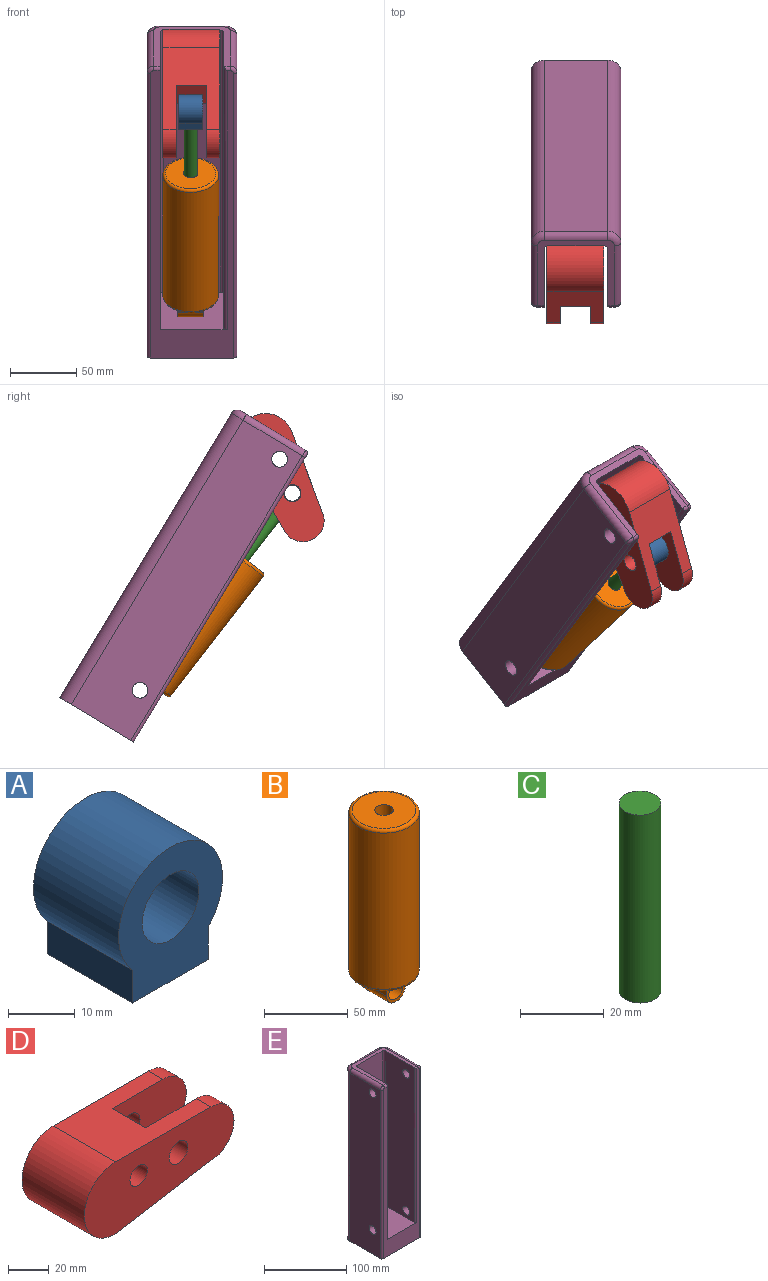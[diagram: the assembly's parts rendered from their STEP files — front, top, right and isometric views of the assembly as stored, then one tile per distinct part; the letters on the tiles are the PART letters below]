
ASSEMBLY  parts=5 mates=5
PART A: 7 faces, bbox 22x18x24.6 mm
  f0: cylinder r=11mm len=22mm, axis (0,1,0), area 921.6mm2, adj f1,f3,f5,f6
  f1: plane 18x6mm, normal (-1,0,0), area 108mm2, adj f0,f2,f5,f6
  f2: plane 18x16mm, normal (0,0,-1), area 288mm2, adj f1,f3,f5,f6
  f3: plane 18x6mm, normal (1,0,0), area 108mm2, adj f0,f2,f5,f6
  f4: cylinder r=6mm len=18mm, axis (0,1,0), area 678.6mm2, adj f5,f6
  f5: plane 24.55x22mm, normal (0,-1,0), area 324.9mm2, adj f0,f1,f2,f3,f4
  f6: plane 24.55x22mm, normal (0,1,0), area 324.9mm2, adj f0,f1,f2,f3,f4
PART B: 13 faces, bbox 45.6x45.6x135 mm
  f0: cylinder r=21.05mm len=114.1mm, axis (0,0,-1), area 15091mm2, adj f3,f4
  f1: plane 38.1x38.1mm, normal (0,0,1), area 1045.1mm2, adj f4,f5
  f2: plane 38.1x38.1mm, normal (0,0,-1), area 820.1mm2, adj f3,f7,f8,f9,f10
  f3: torus R=19.05mm, axis (0,0,1), area 401.2mm2, adj f0,f2
  f4: torus R=19.05mm, axis (0,0,1), area 401.2mm2, adj f0,f1
  f5: cylinder r=5.5mm len=56.1mm, axis (0,0,1), area 1938.7mm2, adj f1,f6
  f6: plane 11x11mm, normal (0,0,1), area 95mm2, adj f5
  f7: plane 20x8.94mm, normal (-1,0,0), area 178.9mm2, adj f2,f9,f10,f11
  f8: plane 20x8.94mm, normal (1,0,0), area 178.9mm2, adj f2,f9,f10,f11
  f9: plane 16.94x16mm, normal (0,-1,0), area 130.5mm2, adj f2,f7,f8,f11,f12
  f10: plane 16.94x16mm, normal (0,1,0), area 130.5mm2, adj f2,f7,f8,f11,f12
  f11: cylinder r=8mm len=20mm, axis (0,1,0), area 502.7mm2, adj f7,f8,f9,f10
  f12: cylinder r=6mm len=20mm, axis (0,1,0), area 754mm2, adj f9,f10
PART C: 3 faces, bbox 10x10x55 mm
  f0: cylinder r=5mm len=55mm, axis (0,0,-1), area 1727.9mm2, adj f1,f2
  f1: plane 10x10mm, normal (0,0,1), area 78.5mm2, adj f0
  f2: plane 10x10mm, normal (0,0,-1), area 78.5mm2, adj f0
PART D: 13 faces, bbox 103.3x43x43 mm
  f0: plane 65.77x43mm, normal (0,0,1), area 2023.1mm2, adj f2,f3,f6,f8,f9,f10,f11,f12
  f1: plane 65.77x43mm, normal (0.16,0,-0.99), area 2051.2mm2, adj f2,f3,f6,f8,f9,f10,f11,f12
  f2: cylinder r=16mm len=32mm, axis (0,1,0), area 502.7mm2, adj f0,f1,f8,f11
  f3: cylinder r=16mm len=32mm, axis (0,1,0), area 502.7mm2, adj f0,f1,f9,f12
  f4: cylinder r=6.46mm len=12.92mm, axis (0,1,0), area 405.7mm2, adj f8,f11
  f5: cylinder r=6.46mm len=12.92mm, axis (0,1,0), area 405.7mm2, adj f9,f12
  f6: cylinder r=21.5mm len=43mm, axis (0,1,0), area 2904.4mm2, adj f0,f1,f8,f9
  f7: cylinder r=6mm len=43mm, axis (0,1,0), area 1621.1mm2, adj f8,f9
  f8: plane 103.27x43mm, normal (0,-1,0), area 3350.4mm2, adj f0,f1,f2,f4,f6,f7
  f9: plane 103.27x43mm, normal (0,1,0), area 3350.4mm2, adj f0,f1,f3,f5,f6,f7
  f10: plane 37.85x23mm, normal (1,0,0), area 870.6mm2, adj f0,f1,f11,f12
  f11: plane 51x37.85mm, normal (0,1,0), area 1493.6mm2, adj f0,f1,f2,f4,f10
  f12: plane 51x37.85mm, normal (0,-1,0), area 1493.6mm2, adj f0,f1,f3,f5,f10
PART E: 30 faces, bbox 69.6x65.8x256.4 mm
  f0: plane 231x52.5mm, normal (1,0,0), area 11900mm2, adj f1,f5,f11,f13,f15,f16,f25
  f1: cylinder r=2.5mm len=231mm, axis (0,0,-1), area 907.1mm2, adj f0,f2,f11,f15
  f2: plane 231x43mm, normal (0,-1,0), area 9933mm2, adj f1,f3,f11,f15
  f3: cylinder r=2.5mm len=231mm, axis (0,0,-1), area 907.1mm2, adj f2,f4,f11,f15
  f4: plane 231x50mm, normal (-1,0,0), area 11323.8mm2, adj f3,f11,f14,f15,f17,f28
  f5: plane 253.5x63mm, normal (0,-1,0), area 4428.6mm2, adj f0,f12,f15,f23,f24,f25,f26,f27
  f6: plane 251x52.5mm, normal (1,0,0), area 12951.3mm2, adj f7,f12,f14,f17,f22,f26
  f7: cylinder r=10mm len=251mm, axis (0,0,-1), area 3942.7mm2, adj f6,f8,f12,f21
  f8: plane 251x48mm, normal (0,1,0), area 12048mm2, adj f7,f9,f12,f20
  f9: cylinder r=10mm len=251mm, axis (0,0,-1), area 3942.7mm2, adj f8,f10,f12,f19
  f10: plane 251x52.5mm, normal (-1,0,0), area 12951.3mm2, adj f9,f12,f13,f16,f18,f23
  f11: plane 58x57.5mm, normal (0,0,1), area 807mm2, adj f0,f1,f2,f3,f4,f18,f19,f20
  f12: plane 68x65mm, normal (0,0,-1), area 4374.4mm2, adj f5,f6,f7,f8,f9,f10,f23,f26
  f13: cylinder r=6mm len=12mm, axis (-1,0,0), area 377mm2, adj f0,f10
  f14: cylinder r=6mm len=12mm, axis (-1,0,0), area 377mm2, adj f4,f6
  f15: plane 55x50.5mm, normal (0,0,1), area 2638.7mm2, adj f0,f1,f2,f3,f4,f5,f28
  f16: cylinder r=6mm len=12mm, axis (-1,0,0), area 377mm2, adj f0,f10
  f17: cylinder r=6mm len=12mm, axis (-1,0,0), area 377mm2, adj f4,f6
  f18: cylinder r=5mm len=52.5mm, axis (0,1,0), area 412.3mm2, adj f10,f11,f19,f24
  f19: torus R=5mm, axis (0,0,1), area 101mm2, adj f9,f11,f18,f20
  f20: cylinder r=5mm len=48mm, axis (1,0,0), area 377mm2, adj f8,f11,f19,f21
  f21: torus R=5mm, axis (0,0,1), area 101mm2, adj f7,f11,f20,f22
  f22: cylinder r=5mm len=52.5mm, axis (0,-1,0), area 412.3mm2, adj f6,f11,f21,f27
  f23: cylinder r=2.5mm len=251mm, axis (0,0,-1), area 985.7mm2, adj f5,f10,f12,f24
  f24: torus R=2.5mm, axis (0,-1,0), area 25.2mm2, adj f5,f18,f23,f25
  f25: cylinder r=2.5mm len=5mm, axis (1,0,0), area 19.6mm2, adj f0,f5,f11,f24
  f26: cylinder r=2.5mm len=251mm, axis (0,0,-1), area 985.7mm2, adj f5,f6,f12,f27
  f27: torus R=2.5mm, axis (0,-1,0), area 25.2mm2, adj f5,f22,f26,f29
  f28: cylinder r=2.5mm len=231mm, axis (0,0,-1), area 903.6mm2, adj f4,f5,f15,f29
  f29: cylinder r=2.5mm len=5mm, axis (-1,0,0), area 16.1mm2, adj f5,f11,f27,f28
PLACE A rot(axis=(0.31,0.31,-0.9),96deg) t=(-28.55,61.52,172.55)mm
PLACE B rot(axis=(0.31,0.31,-0.9),96deg) t=(-28.55,71.71,81.24)mm
PLACE C rot(axis=(0.31,0.31,-0.9),96deg) t=(-28.55,76.18,75.46)mm
PLACE D rot(axis=(0.49,0.49,-0.72),108.8deg) t=(-28.05,4.95,149.32)mm
PLACE E rot(axis=(1,0,0),31.1deg) t=(-29.74,80.11,114.88)mm fixed
MATE revolute A.f0 <-> D.f4  axis (1,0,0) through (-19.55,-1.87,176.4)mm
MATE revolute E.f13 <-> B.f11  axis (-1,0,0) through (-61.55,113.3,27.45)mm
MATE slider B.f5 <-> C.f0  axis (0,-0.61,0.79) through (-28.55,35.59,127.96)mm
MATE fastened A.f2 <-> C.f0  axis (0,0.61,-0.79) through (-28.55,6.41,165.68)mm
MATE revolute D.f7 <-> E.f16  axis (-1,0,0) through (-49.55,7.89,202.11)mm
